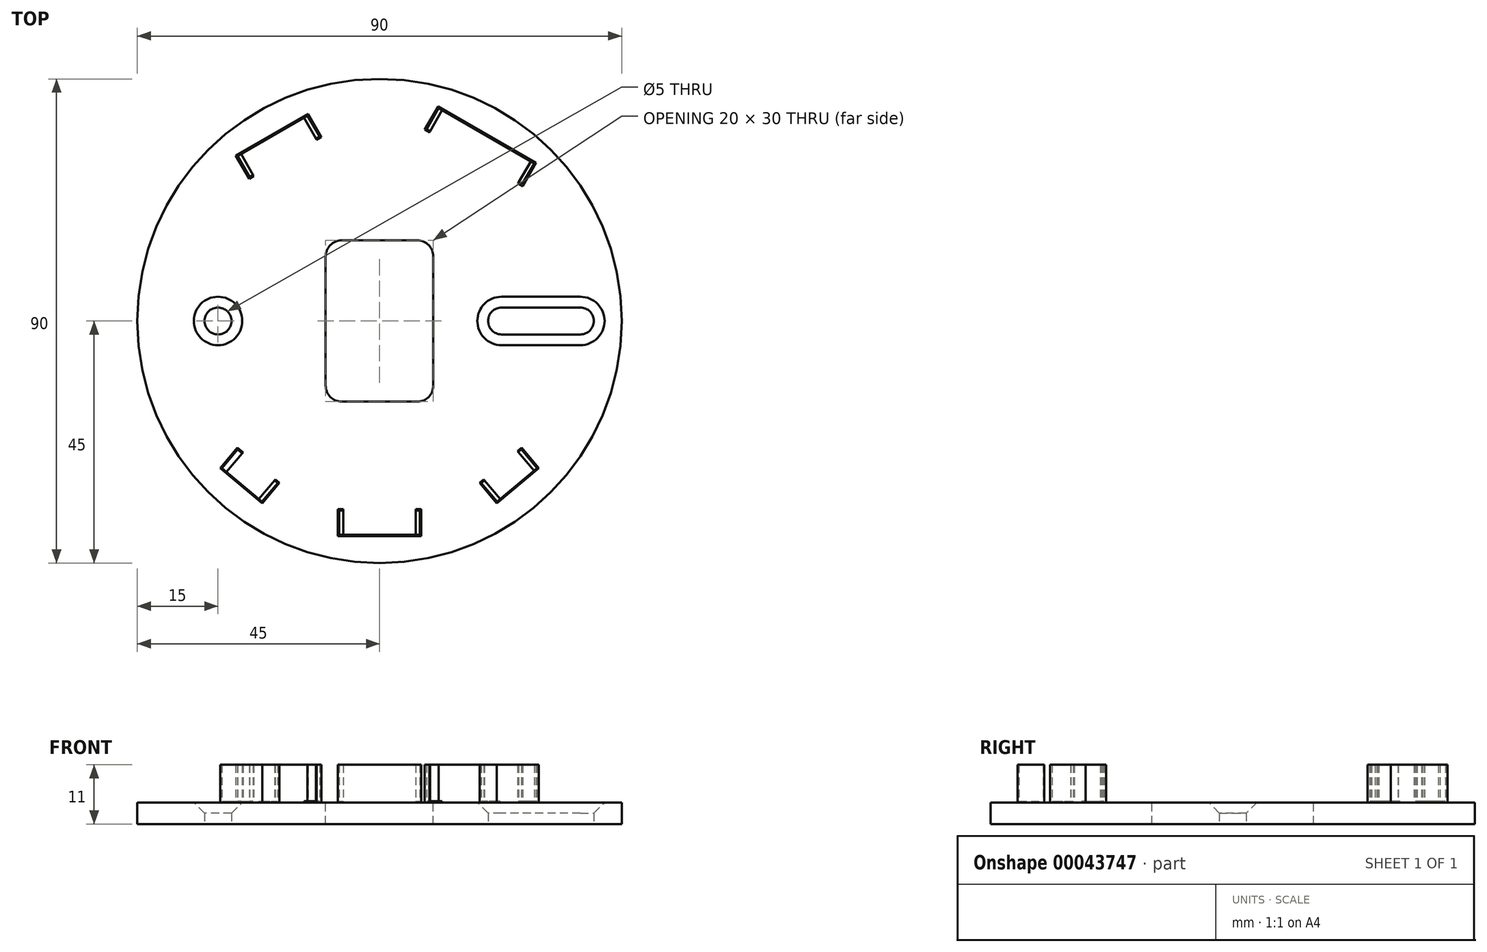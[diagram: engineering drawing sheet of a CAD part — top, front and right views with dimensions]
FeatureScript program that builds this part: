
annotation { "Feature Type Name" : "Feature", "Feature Type Description" : "" }
export const myFeature = defineFeature(function(context is Context, id is Id, definition is map)
    precondition{}
    {
        {
            var Q0;
            Q0=qCreatedBy(makeId("Top.planeOp"),FACE);
            var sketch = newSketch(context, id + "F0", { "sketchPlane" : qUnion([Q0])});
            skCircle(sketch, "E0", {"center": v(0, 0) * mm, "radius": 45 * mm});
            skPoint(sketch, "E1", {"position": v(-30, 0) * mm});
            skPoint(sketch, "E2.MirrorP", {"position": v(30, 0) * mm});
            skCircle(sketch, "E3", {"center": v(-30, 0) * mm, "radius": 2.5 * mm});
            skArc(sketch, "E4", {"start": v(22.68, 2.5) * mm, "mid": v(20.18, 0) * mm, "end": v(22.68, -2.5) * mm});
            skLineSegment(sketch, "E5", {"start": v(30, 0) * mm, "end": v(30, 17.82) * mm, "construction": true});
            skArc(sketch, "E6.MirrorC", {"start": v(37.32, 2.5) * mm, "mid": v(39.82, 0) * mm, "end": v(37.32, -2.5) * mm});
            skLineSegment(sketch, "E7", {"start": v(22.68, 2.5) * mm, "end": v(37.32, 2.5) * mm});
            skLineSegment(sketch, "E8", {"start": v(22.68, -2.5) * mm, "end": v(37.32, -2.5) * mm});
            skSolve(sketch);
        }
        {
            var Q0;
            Q0=makeQuery(id+"F0.imprint","IMPRINT",FACE,{"disambiguationData":[TD([[makeQuery(id+"F0.imprint","IMPRINT",EDGE,{"derivedFrom":sQuery(id+"F0.wireOp",EDGE,"E0")}),1.0]])]});
            extrude(context, id + "F1", {"entities" : qUnion([Q0]), "endBound" : BoundingType.SYMMETRIC, "depth" : 4 * mm});
        }
        {
            var Q0;
            Q0=makeQuery(id+"F1.opExtrude","CAP_EDGE",EDGE,{"disambiguationData":[OSD([sQuery(id+"F0.wireOp",EDGE,"E3")])],"isStart":false});
            chamfer(context, id + "F2", {"entities" : qUnion([Q0]), "chamferType" : ChamferType.OFFSET_ANGLE, "width" : 2 * mm, "oppositeDirection" : false, "angle" : 45 * degree, "tangentPropagation" : true});
        }
        {
            var Q0;
            Q0=makeQuery(id+"F1.opExtrude","CAP_EDGE",EDGE,{"disambiguationData":[OSD([sQuery(id+"F0.wireOp",EDGE,"E4")])],"isStart":false});
            chamfer(context, id + "F3", {"entities" : qUnion([Q0]), "chamferType" : ChamferType.OFFSET_ANGLE, "width" : 2 * mm, "oppositeDirection" : false, "angle" : 45 * degree, "tangentPropagation" : true});
        }
        {
            var Q0;
            Q0=makeQuery(id+"F1.opExtrude","CAP_FACE",FACE,{"disambiguationData":[OSD([sQuery(id+"F0.wireOp",EDGE,"E0"),sQuery(id+"F0.wireOp",EDGE,"E3"),sQuery(id+"F0.wireOp",EDGE,"E4"),sQuery(id+"F0.wireOp",EDGE,"E6.MirrorC"),sQuery(id+"F0.wireOp",EDGE,"E7"),sQuery(id+"F0.wireOp",EDGE,"E8")])],"isStart":false});
            var sketch = newSketch(context, id + "F4", { "sketchPlane" : qUnion([Q0])});
            skLineSegment(sketch, "E9.rect.bottom", {"start": v(29.1, 29.4) * mm, "end": v(10.9, 39.9) * mm});
            skLineSegment(sketch, "E9.rect.top", {"start": v(26.6, 25.06) * mm, "end": v(8.4, 35.56) * mm});
            skLineSegment(sketch, "E9.rect.left", {"start": v(29.1, 29.4) * mm, "end": v(26.6, 25.06) * mm});
            skLineSegment(sketch, "E9.rect.right", {"start": v(10.9, 39.9) * mm, "end": v(8.4, 35.56) * mm});
            skPoint(sketch, "E9.rect.middle", {"position": v(18.75, 32.48) * mm});
            skLineSegment(sketch, "E10", {"start": v(17.5, 30.31) * mm, "end": v(0, 0) * mm, "construction": true});
            skSolve(sketch);
        }
        {
            var Q0;
            Q0=makeQuery(id+"F4.imprint","IMPRINT",FACE,{"disambiguationData":[TD([[makeQuery(id+"F4.imprint","IMPRINT",EDGE,{"derivedFrom":sQuery(id+"F4.wireOp",EDGE,"E9.rect.bottom")}),-1.0]])]});
            var sketch = newSketch(context, id + "F5", { "sketchPlane" : qUnion([Q0])});
            skLineSegment(sketch, "E11.rect.bottom", {"start": v(-13.29, 38.52) * mm, "end": v(-26.71, 30.77) * mm});
            skLineSegment(sketch, "E11.rect.top", {"start": v(-10.79, 34.19) * mm, "end": v(-24.21, 26.44) * mm});
            skLineSegment(sketch, "E11.rect.left", {"start": v(-13.29, 38.52) * mm, "end": v(-10.79, 34.19) * mm});
            skLineSegment(sketch, "E11.rect.right", {"start": v(-26.71, 30.77) * mm, "end": v(-24.21, 26.44) * mm});
            skPoint(sketch, "E11.rect.middle", {"position": v(-18.75, 32.48) * mm});
            skLineSegment(sketch, "E12", {"start": v(-17.5, 30.31) * mm, "end": v(0, 0) * mm, "construction": true});
            skSolve(sketch);
        }
        {
            var Q0;
            Q0=makeQuery(id+"F4.imprint","IMPRINT",FACE,{"disambiguationData":[TD([[makeQuery(id+"F4.imprint","IMPRINT",EDGE,{"derivedFrom":sQuery(id+"F4.wireOp",EDGE,"E9.rect.bottom")}),-1.0]])]});
            var sketch = newSketch(context, id + "F6", { "sketchPlane" : qUnion([Q0])});
            skLineSegment(sketch, "E13.rect.bottom", {"start": v(-7.75, -40) * mm, "end": v(7.75, -40) * mm});
            skLineSegment(sketch, "E13.rect.top", {"start": v(-7.75, -35) * mm, "end": v(7.75, -35) * mm});
            skLineSegment(sketch, "E13.rect.left", {"start": v(-7.75, -40) * mm, "end": v(-7.75, -35) * mm});
            skLineSegment(sketch, "E13.rect.right", {"start": v(7.75, -40) * mm, "end": v(7.75, -35) * mm});
            skPoint(sketch, "E13.rect.middle", {"position": v(0, -37.5) * mm});
            skLineSegment(sketch, "E14", {"start": v(0, -35) * mm, "end": v(0, 0) * mm, "construction": true});
            skSolve(sketch);
        }
        {
            var Q0;
            Q0=makeQuery(id+"F4.imprint","IMPRINT",FACE,{"disambiguationData":[TD([[makeQuery(id+"F4.imprint","IMPRINT",EDGE,{"derivedFrom":sQuery(id+"F4.wireOp",EDGE,"E9.rect.bottom")}),-1.0]])]});
            var sketch = newSketch(context, id + "F7", { "sketchPlane" : qUnion([Q0])});
            skLineSegment(sketch, "E15.rect.bottom", {"start": v(-29.62, -27.36) * mm, "end": v(-21.8, -33.92) * mm});
            skLineSegment(sketch, "E15.rect.top", {"start": v(-26.4, -23.53) * mm, "end": v(-18.6, -30.09) * mm});
            skLineSegment(sketch, "E15.rect.left", {"start": v(-29.62, -27.36) * mm, "end": v(-26.4, -23.53) * mm});
            skLineSegment(sketch, "E15.rect.right", {"start": v(-21.8, -33.92) * mm, "end": v(-18.6, -30.09) * mm});
            skPoint(sketch, "E15.rect.middle", {"position": v(-24.1, -28.73) * mm});
            skLineSegment(sketch, "E16", {"start": v(-22.5, -26.81) * mm, "end": v(0, 0) * mm, "construction": true});
            skSolve(sketch);
        }
        {
            var Q0;
            Q0=makeQuery(id+"F4.imprint","IMPRINT",FACE,{"disambiguationData":[TD([[makeQuery(id+"F4.imprint","IMPRINT",EDGE,{"derivedFrom":sQuery(id+"F4.wireOp",EDGE,"E9.rect.bottom")}),-1.0]])]});
            var sketch = newSketch(context, id + "F8", { "sketchPlane" : qUnion([Q0])});
            skLineSegment(sketch, "E17.rect.bottom", {"start": v(21.8, -33.92) * mm, "end": v(29.62, -27.36) * mm});
            skLineSegment(sketch, "E17.rect.top", {"start": v(18.6, -30.09) * mm, "end": v(26.4, -23.53) * mm});
            skLineSegment(sketch, "E17.rect.left", {"start": v(21.8, -33.92) * mm, "end": v(18.6, -30.09) * mm});
            skLineSegment(sketch, "E17.rect.right", {"start": v(29.62, -27.36) * mm, "end": v(26.4, -23.53) * mm});
            skPoint(sketch, "E17.rect.middle", {"position": v(24.1, -28.73) * mm});
            skLineSegment(sketch, "E18", {"start": v(22.5, -26.81) * mm, "end": v(0, 0) * mm, "construction": true});
            skSolve(sketch);
        }
        {
            var Q0;
            Q0 = qSketchRegion(id + "F4", true);
            var Q1;
            Q1 = qSketchRegion(id + "F5", true);
            var Q2;
            Q2 = qSketchRegion(id + "F6", true);
            var Q3;
            Q3 = qSketchRegion(id + "F7", true);
            var Q4;
            Q4 = qSketchRegion(id + "F8", true);
            extrude(context, id + "F9", {"entities" : qUnion([Q0, Q1, Q2, Q3, Q4]), "depth" : 7 * mm});
        }
        {
            var Q0;
            Q0=makeQuery(id+"F9.opExtrude","CAP_FACE",FACE,{"disambiguationData":[OSD([sQuery(id+"F5.wireOp",EDGE,"E11.rect.bottom"),sQuery(id+"F5.wireOp",EDGE,"E11.rect.top"),sQuery(id+"F5.wireOp",EDGE,"E11.rect.left"),sQuery(id+"F5.wireOp",EDGE,"E11.rect.right")])],"isStart":false});
            var Q1;
            Q1=makeQuery(id+"F9.opExtrude","CAP_FACE",FACE,{"disambiguationData":[OSD([sQuery(id+"F4.wireOp",EDGE,"E9.rect.bottom"),sQuery(id+"F4.wireOp",EDGE,"E9.rect.top"),sQuery(id+"F4.wireOp",EDGE,"E9.rect.left"),sQuery(id+"F4.wireOp",EDGE,"E9.rect.right")])],"isStart":false});
            var Q2;
            Q2=makeQuery(id+"F9.opExtrude","CAP_FACE",FACE,{"disambiguationData":[OSD([sQuery(id+"F8.wireOp",EDGE,"E17.rect.bottom"),sQuery(id+"F8.wireOp",EDGE,"E17.rect.top"),sQuery(id+"F8.wireOp",EDGE,"E17.rect.left"),sQuery(id+"F8.wireOp",EDGE,"E17.rect.right")])],"isStart":false});
            var Q3;
            Q3=makeQuery(id+"F9.opExtrude","CAP_FACE",FACE,{"disambiguationData":[OSD([sQuery(id+"F6.wireOp",EDGE,"E13.rect.bottom"),sQuery(id+"F6.wireOp",EDGE,"E13.rect.top"),sQuery(id+"F6.wireOp",EDGE,"E13.rect.left"),sQuery(id+"F6.wireOp",EDGE,"E13.rect.right")])],"isStart":false});
            var Q4;
            Q4=makeQuery(id+"F9.opExtrude","CAP_FACE",FACE,{"disambiguationData":[OSD([sQuery(id+"F7.wireOp",EDGE,"E15.rect.bottom"),sQuery(id+"F7.wireOp",EDGE,"E15.rect.top"),sQuery(id+"F7.wireOp",EDGE,"E15.rect.left"),sQuery(id+"F7.wireOp",EDGE,"E15.rect.right")])],"isStart":false});
            shell(context, id + "F10", {"entities" : qUnion([Q0, Q1, Q2, Q3, Q4]), "thickness" : 0.25 * mm});
        }
        {
            var Q0;
            Q0=makeQuery(id+"F9.opExtrude","SWEPT_FACE",FACE,{"disambiguationData":[OSD([sQuery(id+"F5.wireOp",EDGE,"E11.rect.top")])]});
            var sketch = newSketch(context, id + "F11", { "sketchPlane" : qUnion([Q0])});
            skLineSegment(sketch, "E19.bottom", {"start": v(-6.75, 9) * mm, "end": v(6.75, 9) * mm});
            skLineSegment(sketch, "E19.top", {"start": v(-6.75, 2) * mm, "end": v(6.75, 2) * mm});
            skLineSegment(sketch, "E19.left", {"start": v(-6.75, 9) * mm, "end": v(-6.75, 2) * mm});
            skLineSegment(sketch, "E19.right", {"start": v(6.75, 9) * mm, "end": v(6.75, 2) * mm});
            skSolve(sketch);
        }
        {
            var Q0;
            Q0=makeQuery(id+"F11.imprint","IMPRINT",FACE,{"disambiguationData":[TD([[makeQuery(id+"F11.imprint","IMPRINT",EDGE,{"derivedFrom":sQuery(id+"F11.wireOp",EDGE,"E19.bottom")}),1.0]])]});
            var Q1;
            Q1=makeQuery(id+"F10.opShell","OFFSET_FACE",FACE,{"disambiguationData":[OSD([sQuery(id+"F5.wireOp",EDGE,"E11.rect.bottom")])]});
            extrude(context, id + "F12", {"entities" : qUnion([Q0]), "operationType" : NewBodyOperationType.REMOVE, "endBound" : BoundingType.UP_TO_SURFACE, "oppositeDirection" : true, "endBoundEntityFace" : qUnion([Q1]), "depth" : 25 * mm});
        }
        {
            var Q0;
            Q0=makeQuery(id+"F9.opExtrude","SWEPT_FACE",FACE,{"disambiguationData":[OSD([sQuery(id+"F4.wireOp",EDGE,"E9.rect.top")])]});
            var sketch = newSketch(context, id + "F13", { "sketchPlane" : qUnion([Q0])});
            skLineSegment(sketch, "E20.bottom", {"start": v(-9.5, 9) * mm, "end": v(9.5, 9) * mm});
            skLineSegment(sketch, "E20.top", {"start": v(-9.5, 2) * mm, "end": v(9.5, 2) * mm});
            skLineSegment(sketch, "E20.left", {"start": v(-9.5, 9) * mm, "end": v(-9.5, 2) * mm});
            skLineSegment(sketch, "E20.right", {"start": v(9.5, 9) * mm, "end": v(9.5, 2) * mm});
            skSolve(sketch);
        }
        {
            var Q0;
            Q0=makeQuery(id+"F13.imprint","IMPRINT",FACE,{"disambiguationData":[TD([[makeQuery(id+"F13.imprint","IMPRINT",EDGE,{"derivedFrom":sQuery(id+"F13.wireOp",EDGE,"E20.bottom")}),1.0]])]});
            var Q1;
            Q1=makeQuery(id+"F10.opShell","OFFSET_FACE",FACE,{"disambiguationData":[OSD([sQuery(id+"F4.wireOp",EDGE,"E9.rect.bottom")])]});
            extrude(context, id + "F14", {"entities" : qUnion([Q0]), "operationType" : NewBodyOperationType.REMOVE, "endBound" : BoundingType.UP_TO_SURFACE, "oppositeDirection" : true, "endBoundEntityFace" : qUnion([Q1]), "depth" : 25 * mm});
        }
        {
            var Q0;
            Q0=makeQuery(id+"F9.opExtrude","SWEPT_FACE",FACE,{"disambiguationData":[OSD([sQuery(id+"F8.wireOp",EDGE,"E17.rect.top")])]});
            var sketch = newSketch(context, id + "F15", { "sketchPlane" : qUnion([Q0])});
            skLineSegment(sketch, "E21.bottom", {"start": v(-4.1, 9) * mm, "end": v(4.1, 9) * mm});
            skLineSegment(sketch, "E21.top", {"start": v(-4.1, 2) * mm, "end": v(4.1, 2) * mm});
            skLineSegment(sketch, "E21.left", {"start": v(-4.1, 9) * mm, "end": v(-4.1, 2) * mm});
            skLineSegment(sketch, "E21.right", {"start": v(4.1, 9) * mm, "end": v(4.1, 2) * mm});
            skSolve(sketch);
        }
        {
            var Q0;
            Q0=makeQuery(id+"F15.imprint","IMPRINT",FACE,{"disambiguationData":[TD([[makeQuery(id+"F15.imprint","IMPRINT",EDGE,{"derivedFrom":sQuery(id+"F15.wireOp",EDGE,"E21.bottom")}),1.0]])]});
            var Q1;
            Q1=makeQuery(id+"F10.opShell","OFFSET_FACE",FACE,{"disambiguationData":[OSD([sQuery(id+"F8.wireOp",EDGE,"E17.rect.bottom")])]});
            extrude(context, id + "F16", {"entities" : qUnion([Q0]), "operationType" : NewBodyOperationType.REMOVE, "endBound" : BoundingType.UP_TO_SURFACE, "oppositeDirection" : true, "endBoundEntityFace" : qUnion([Q1]), "depth" : 25 * mm});
        }
        {
            var Q0;
            Q0=makeQuery(id+"F9.opExtrude","SWEPT_FACE",FACE,{"disambiguationData":[OSD([sQuery(id+"F6.wireOp",EDGE,"E13.rect.top")])]});
            var sketch = newSketch(context, id + "F17", { "sketchPlane" : qUnion([Q0])});
            skLineSegment(sketch, "E22.bottom", {"start": v(-6.75, 9) * mm, "end": v(6.75, 9) * mm});
            skLineSegment(sketch, "E22.top", {"start": v(-6.75, 2) * mm, "end": v(6.75, 2) * mm});
            skLineSegment(sketch, "E22.left", {"start": v(-6.75, 9) * mm, "end": v(-6.75, 2) * mm});
            skLineSegment(sketch, "E22.right", {"start": v(6.75, 9) * mm, "end": v(6.75, 2) * mm});
            skSolve(sketch);
        }
        {
            var Q0;
            Q0=makeQuery(id+"F17.imprint","IMPRINT",FACE,{"disambiguationData":[TD([[makeQuery(id+"F17.imprint","IMPRINT",EDGE,{"derivedFrom":sQuery(id+"F17.wireOp",EDGE,"E22.bottom")}),1.0]])]});
            var Q1;
            Q1=makeQuery(id+"F10.opShell","OFFSET_FACE",FACE,{"disambiguationData":[OSD([sQuery(id+"F6.wireOp",EDGE,"E13.rect.bottom")])]});
            extrude(context, id + "F18", {"entities" : qUnion([Q0]), "operationType" : NewBodyOperationType.REMOVE, "endBound" : BoundingType.UP_TO_SURFACE, "oppositeDirection" : true, "endBoundEntityFace" : qUnion([Q1]), "depth" : 25 * mm});
        }
        {
            var Q0;
            Q0=makeQuery(id+"F9.opExtrude","SWEPT_FACE",FACE,{"disambiguationData":[OSD([sQuery(id+"F7.wireOp",EDGE,"E15.rect.top")])]});
            var sketch = newSketch(context, id + "F19", { "sketchPlane" : qUnion([Q0])});
            skLineSegment(sketch, "E23.bottom", {"start": v(-4.1, 9) * mm, "end": v(3.73, 9) * mm});
            skLineSegment(sketch, "E23.top", {"start": v(-4.1, 2) * mm, "end": v(3.73, 2) * mm});
            skLineSegment(sketch, "E23.left", {"start": v(-4.1, 9) * mm, "end": v(-4.1, 2) * mm});
            skLineSegment(sketch, "E23.right", {"start": v(3.73, 9) * mm, "end": v(3.73, 2) * mm});
            skSolve(sketch);
        }
        {
            var Q0;
            Q0=makeQuery(id+"F19.imprint","IMPRINT",FACE,{"disambiguationData":[TD([[makeQuery(id+"F19.imprint","IMPRINT",EDGE,{"derivedFrom":sQuery(id+"F19.wireOp",EDGE,"E23.bottom")}),1.0]])]});
            var Q1;
            Q1=makeQuery(id+"F10.opShell","OFFSET_FACE",FACE,{"disambiguationData":[OSD([sQuery(id+"F7.wireOp",EDGE,"E15.rect.bottom")])]});
            extrude(context, id + "F20", {"entities" : qUnion([Q0]), "operationType" : NewBodyOperationType.REMOVE, "endBound" : BoundingType.UP_TO_SURFACE, "oppositeDirection" : true, "endBoundEntityFace" : qUnion([Q1]), "depth" : 25 * mm});
        }
        {
            var Q0;
            Q0=makeQuery(id+"F1.opExtrude","CAP_FACE",FACE,{"disambiguationData":[OSD([sQuery(id+"F0.wireOp",EDGE,"E0"),sQuery(id+"F0.wireOp",EDGE,"E3"),sQuery(id+"F0.wireOp",EDGE,"E4"),sQuery(id+"F0.wireOp",EDGE,"E6.MirrorC"),sQuery(id+"F0.wireOp",EDGE,"E7"),sQuery(id+"F0.wireOp",EDGE,"E8")])],"isStart":false});
            var sketch = newSketch(context, id + "F21", { "sketchPlane" : qUnion([Q0])});
            skLineSegment(sketch, "E24.rect.bottom", {"start": v(-7, 15) * mm, "end": v(7, 15) * mm});
            skLineSegment(sketch, "E24.rect.top", {"start": v(-7, -15) * mm, "end": v(7, -15) * mm});
            skLineSegment(sketch, "E24.rect.left", {"start": v(-10, 12) * mm, "end": v(-10, -12) * mm});
            skLineSegment(sketch, "E24.rect.right", {"start": v(10, 12) * mm, "end": v(10, -12) * mm});
            skPoint(sketch, "E24.rect.middle", {"position": v(0, 0) * mm});
            skPoint(sketch, "E25.visualSharp", {"position": v(-10, 15) * mm});
            skArc(sketch, "E25.filletArc", {"start": v(-7, 15) * mm, "mid": v(-9.12, 14.12) * mm, "end": v(-10, 12) * mm});
            skPoint(sketch, "E26.visualSharp", {"position": v(10, 15) * mm});
            skArc(sketch, "E26.filletArc", {"start": v(10, 12) * mm, "mid": v(9.12, 14.12) * mm, "end": v(7, 15) * mm});
            skPoint(sketch, "E27.visualSharp", {"position": v(10, -15) * mm});
            skArc(sketch, "E27.filletArc", {"start": v(7, -15) * mm, "mid": v(9.12, -14.12) * mm, "end": v(10, -12) * mm});
            skPoint(sketch, "E28.visualSharp", {"position": v(-10, -15) * mm});
            skArc(sketch, "E28.filletArc", {"start": v(-10, -12) * mm, "mid": v(-9.12, -14.12) * mm, "end": v(-7, -15) * mm});
            skSolve(sketch);
        }
        {
            var Q0;
            Q0=makeQuery(id+"F21.imprint","IMPRINT",FACE,{"disambiguationData":[TD([[makeQuery(id+"F21.imprint","IMPRINT",EDGE,{"derivedFrom":sQuery(id+"F21.wireOp",EDGE,"E24.rect.bottom")}),-1.0]])]});
            extrude(context, id + "F22", {"entities" : qUnion([Q0]), "operationType" : NewBodyOperationType.REMOVE, "endBound" : BoundingType.THROUGH_ALL, "oppositeDirection" : true, "depth" : 25 * mm});
        }
    });
